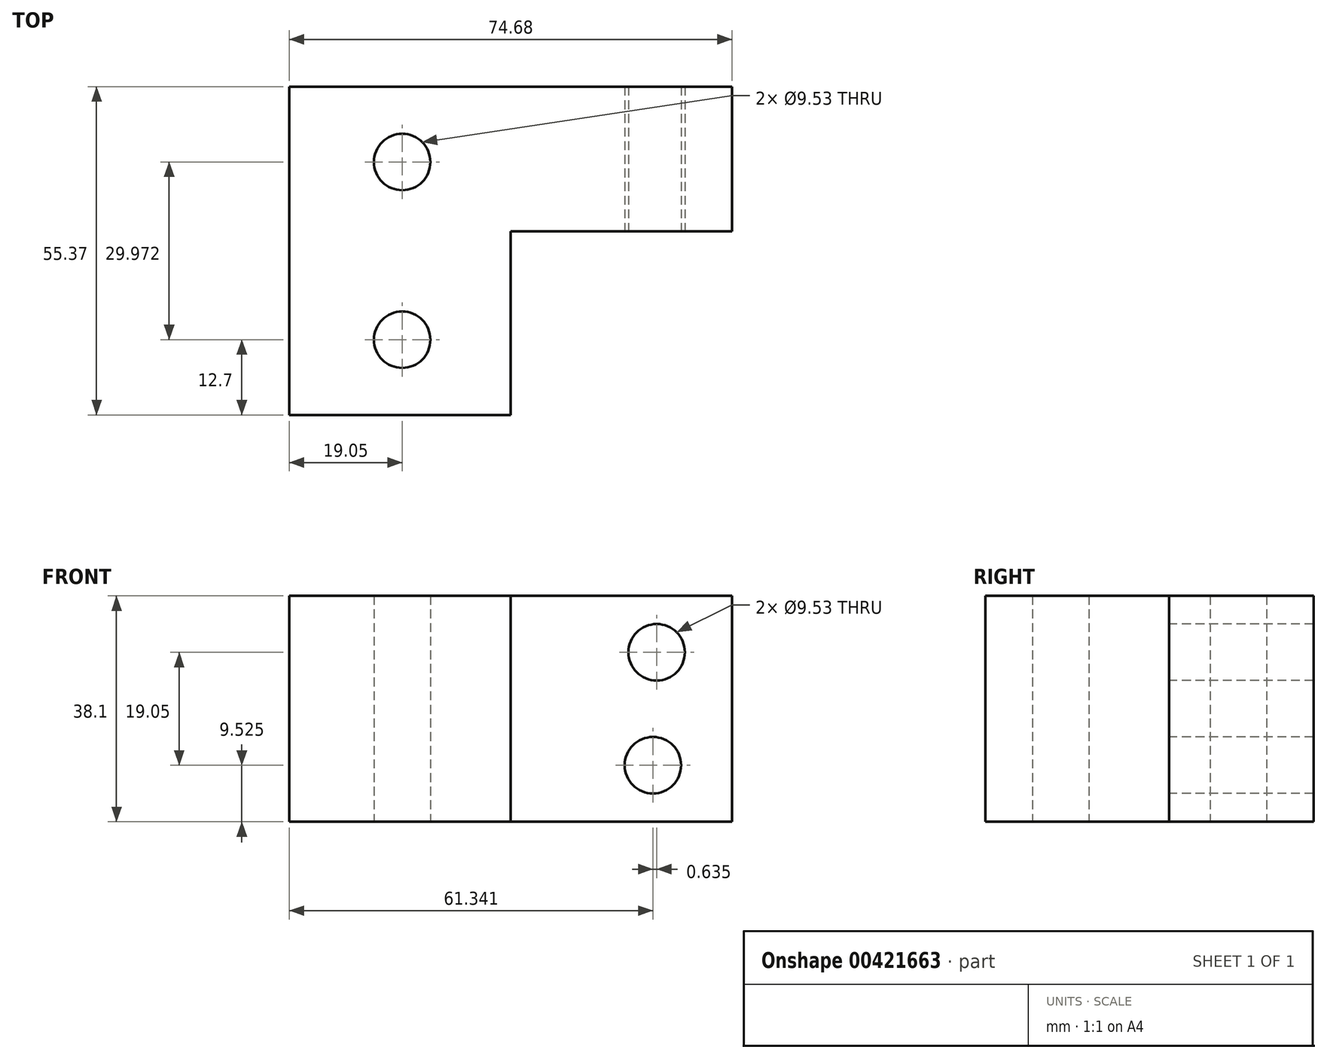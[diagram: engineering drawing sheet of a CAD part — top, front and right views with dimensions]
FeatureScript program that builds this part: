
annotation { "Feature Type Name" : "Feature", "Feature Type Description" : "" }
export const myFeature = defineFeature(function(context is Context, id is Id, definition is map)
    precondition{}
    {
        {
            var Q0;
            Q0=qCreatedBy(makeId("Top.planeOp"),FACE);
            var sketch = newSketch(context, id + "F0", { "sketchPlane" : qUnion([Q0])});
            skLineSegment(sketch, "E0.bottom", {"start": v(0, 0) * mm, "end": v(37.34, 0) * mm});
            skLineSegment(sketch, "E0.top", {"start": v(0, 55.37) * mm, "end": v(37.34, 55.37) * mm});
            skLineSegment(sketch, "E0.left", {"start": v(0, 0) * mm, "end": v(0, 55.37) * mm});
            skLineSegment(sketch, "E0.right", {"start": v(37.34, 0) * mm, "end": v(37.34, 30.99) * mm});
            skLineSegment(sketch, "E1.bottom", {"start": v(37.34, 55.37) * mm, "end": v(74.68, 55.37) * mm});
            skLineSegment(sketch, "E1.top", {"start": v(37.34, 30.99) * mm, "end": v(74.68, 30.99) * mm});
            skLineSegment(sketch, "E1.right", {"start": v(74.68, 55.37) * mm, "end": v(74.68, 30.99) * mm});
            skLineSegment(sketch, "E2", {"start": v(0, 42.67) * mm, "end": v(19.05, 42.67) * mm, "construction": true});
            skLineSegment(sketch, "E3", {"start": v(0, 12.7) * mm, "end": v(19.05, 12.7) * mm, "construction": true});
            skCircle(sketch, "E4", {"center": v(19.05, 42.67) * mm, "radius": 4.76 * mm});
            skCircle(sketch, "E5", {"center": v(19.05, 12.7) * mm, "radius": 4.76 * mm});
            skSolve(sketch);
        }
        {
            var Q0;
            Q0 = qSketchRegion(id + "F0", true);
            extrude(context, id + "F1", {"entities" : qUnion([Q0]), "depth" : 38.1 * mm});
        }
        {
            var Q0;
            Q0=makeQuery(id+"F1.opExtrude","SWEPT_FACE",FACE,{"disambiguationData":[OSD([sQuery(id+"F0.wireOp",EDGE,"E1.top")])]});
            var sketch = newSketch(context, id + "F2", { "sketchPlane" : qUnion([Q0])});
            skLineSegment(sketch, "E6", {"start": v(61.98, 38.1) * mm, "end": v(61.98, 28.58) * mm, "construction": true});
            skLineSegment(sketch, "E7", {"start": v(61.34, 0) * mm, "end": v(61.34, 9.53) * mm, "construction": true});
            skCircle(sketch, "E8", {"center": v(61.98, 28.58) * mm, "radius": 4.76 * mm});
            skCircle(sketch, "E9", {"center": v(61.34, 9.53) * mm, "radius": 4.76 * mm});
            skSolve(sketch);
        }
        {
            var Q0;
            Q0 = qSketchRegion(id + "F2", true);
            var Q1;
            Q1=sQuery(id+"F2.wireOp",EDGE,"E8");
            var Q2;
            Q2=sQuery(id+"F2.wireOp",EDGE,"qypGJX3X-CxUN-YB8d-jImS-mnVKemegrm0G");
            extrude(context, id + "F3", {"entities" : qUnion([Q0]), "operationType" : NewBodyOperationType.REMOVE, "surfaceEntities" : qUnion([Q1, Q2]), "endBound" : BoundingType.THROUGH_ALL, "oppositeDirection" : true, "depth" : 25.4 * mm});
        }
    });
